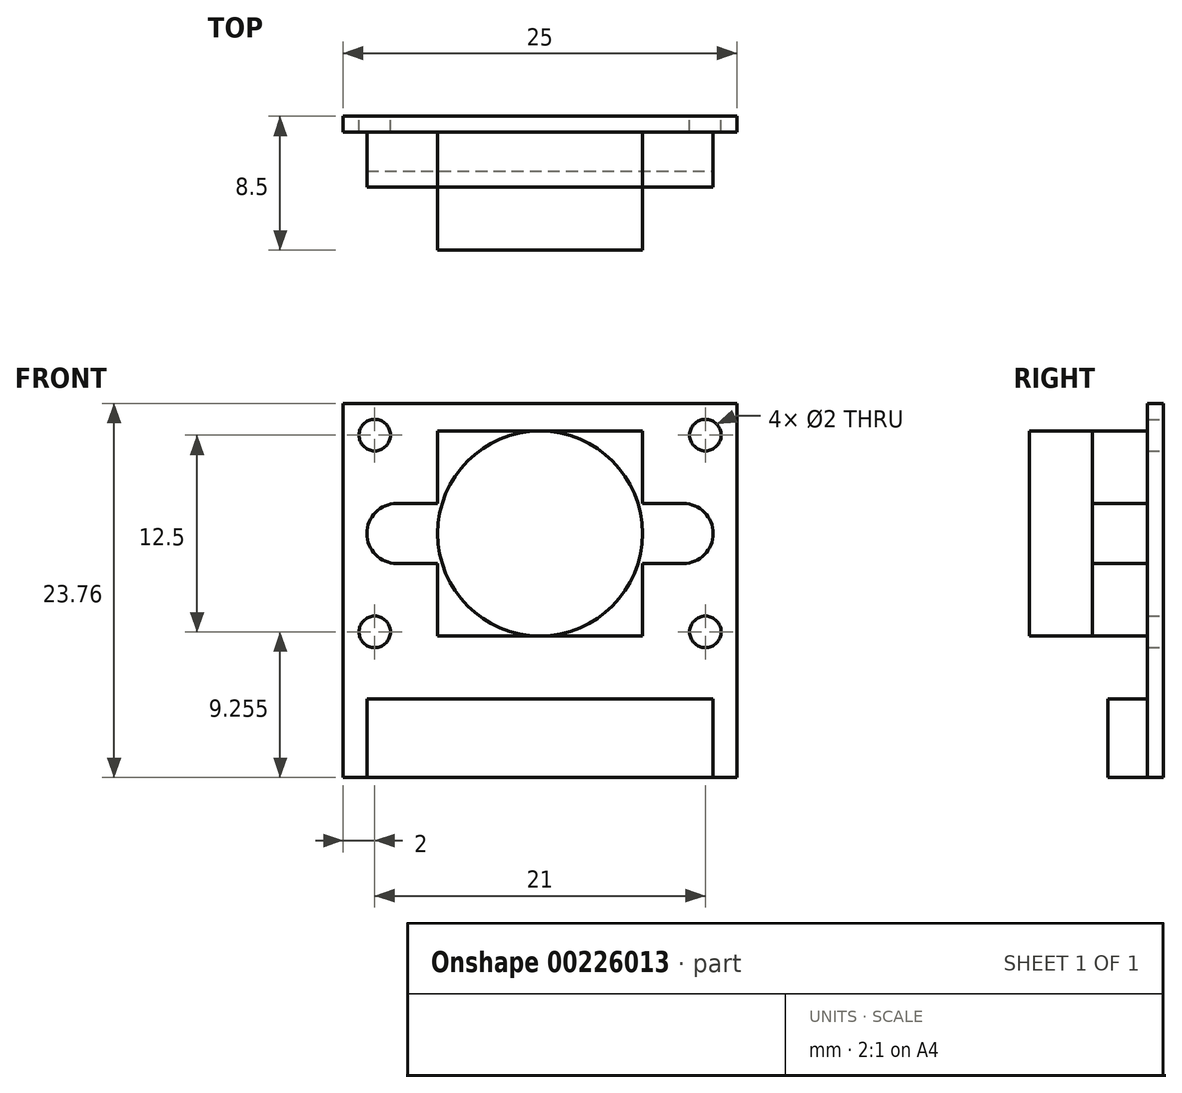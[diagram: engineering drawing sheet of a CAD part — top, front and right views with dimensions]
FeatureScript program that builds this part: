
annotation { "Feature Type Name" : "Feature", "Feature Type Description" : "" }
export const myFeature = defineFeature(function(context is Context, id is Id, definition is map)
    precondition{}
    {
        {
            var Q0;
            Q0=qCreatedBy(makeId("Front.planeOp"),FACE);
            var sketch = newSketch(context, id + "F0", { "sketchPlane" : qUnion([Q0])});
            skLineSegment(sketch, "E0.bottom", {"start": v(-12.5, 11.88) * mm, "end": v(12.5, 11.88) * mm});
            skLineSegment(sketch, "E0.top", {"start": v(-12.5, -11.88) * mm, "end": v(12.5, -11.88) * mm});
            skLineSegment(sketch, "E0.left", {"start": v(-12.5, 11.88) * mm, "end": v(-12.5, -11.87) * mm});
            skLineSegment(sketch, "E0.right", {"start": v(12.5, 11.88) * mm, "end": v(12.5, -11.87) * mm});
            skPoint(sketch, "E0.middle", {"position": v(0, 0) * mm});
            skCircle(sketch, "E1", {"center": v(-10.5, 9.87) * mm, "radius": 1 * mm});
            skLineSegment(sketch, "E2", {"start": v(0, 11.88) * mm, "end": v(0, 0) * mm, "construction": true});
            skCircle(sketch, "E3", {"center": v(-10.5, -2.63) * mm, "radius": 1 * mm});
            skCircle(sketch, "E4.MirrorC", {"center": v(10.5, 9.87) * mm, "radius": 1 * mm});
            skCircle(sketch, "E5.MirrorC", {"center": v(10.5, -2.63) * mm, "radius": 1 * mm});
            skSolve(sketch);
        }
        {
            var Q0;
            Q0 = qSketchRegion(id + "F0", true);
            extrude(context, id + "F1", {"entities" : qUnion([Q0]), "depth" : 1 * mm});
        }
        {
            var Q0;
            Q0=makeQuery(id+"F1.opExtrude","CAP_FACE",FACE,{"disambiguationData":[OSD([sQuery(id+"F0.wireOp",EDGE,"E0.bottom"),sQuery(id+"F0.wireOp",EDGE,"E0.top"),sQuery(id+"F0.wireOp",EDGE,"E0.left"),sQuery(id+"F0.wireOp",EDGE,"E0.right"),sQuery(id+"F0.wireOp",EDGE,"E1"),sQuery(id+"F0.wireOp",EDGE,"E3"),sQuery(id+"F0.wireOp",EDGE,"E4.MirrorC"),sQuery(id+"F0.wireOp",EDGE,"E5.MirrorC")])],"isStart":false});
            var sketch = newSketch(context, id + "F2", { "sketchPlane" : qUnion([Q0])});
            skLineSegment(sketch, "E6.bottom", {"start": v(-11, -11.88) * mm, "end": v(0, -11.88) * mm});
            skLineSegment(sketch, "E6.top", {"start": v(-11, -6.88) * mm, "end": v(0, -6.88) * mm});
            skLineSegment(sketch, "E6.left", {"start": v(-11, -11.88) * mm, "end": v(-11, -6.88) * mm});
            skLineSegment(sketch, "E7", {"start": v(0, 11.88) * mm, "end": v(0, -11.88) * mm, "construction": true});
            skLineSegment(sketch, "E8.MirrorCS", {"start": v(11, -6.88) * mm, "end": v(0, -6.88) * mm});
            skLineSegment(sketch, "E9.MirrorCS", {"start": v(11, -11.88) * mm, "end": v(11, -6.88) * mm});
            skLineSegment(sketch, "E10.MirrorCS", {"start": v(11, -11.88) * mm, "end": v(0, -11.88) * mm});
            skSolve(sketch);
        }
        {
            var Q0;
            Q0 = qSketchRegion(id + "F2", true);
            extrude(context, id + "F3", {"entities" : qUnion([Q0]), "depth" : 2.5 * mm});
        }
        {
            var Q0;
            Q0=makeQuery(id+"F1.opExtrude","CAP_FACE",FACE,{"disambiguationData":[OSD([sQuery(id+"F0.wireOp",EDGE,"E0.bottom"),sQuery(id+"F0.wireOp",EDGE,"E0.top"),sQuery(id+"F0.wireOp",EDGE,"E0.left"),sQuery(id+"F0.wireOp",EDGE,"E0.right"),sQuery(id+"F0.wireOp",EDGE,"E1"),sQuery(id+"F0.wireOp",EDGE,"E3"),sQuery(id+"F0.wireOp",EDGE,"E4.MirrorC"),sQuery(id+"F0.wireOp",EDGE,"E5.MirrorC")])],"isStart":false});
            var sketch = newSketch(context, id + "F4", { "sketchPlane" : qUnion([Q0])});
            skLineSegment(sketch, "E11.bottom", {"start": v(6.5, -2.88) * mm, "end": v(-6.5, -2.88) * mm});
            skLineSegment(sketch, "E11.top", {"start": v(6.5, 10.12) * mm, "end": v(-6.5, 10.12) * mm});
            skLineSegment(sketch, "E11.left", {"start": v(6.5, -2.88) * mm, "end": v(6.5, 1.72) * mm});
            skLineSegment(sketch, "E11.right", {"start": v(-6.5, -2.88) * mm, "end": v(-6.5, 1.72) * mm});
            skPoint(sketch, "E11.middle", {"position": v(0, 3.62) * mm});
            skLineSegment(sketch, "E12", {"start": v(0, 11.88) * mm, "end": v(0, 3.62) * mm, "construction": true});
            skPoint(sketch, "E12.endSnap0", {"position": v(0, 11.88) * mm});
            skLineSegment(sketch, "E13", {"start": v(-10.5, 9.87) * mm, "end": v(-10.5, -2.63) * mm, "construction": true});
            skLineSegment(sketch, "E14", {"start": v(-10.5, 3.62) * mm, "end": v(10.5, 3.62) * mm, "construction": true});
            skLineSegment(sketch, "E15", {"start": v(-9.1, 3.62) * mm, "end": v(9.1, 3.62) * mm, "construction": true});
            skArc(sketch, "E16.0.startCap", {"start": v(-9.1, 1.72) * mm, "mid": v(-11, 3.62) * mm, "end": v(-9.1, 5.52) * mm});
            skArc(sketch, "E16.0.endCap", {"start": v(9.1, 5.52) * mm, "mid": v(11, 3.62) * mm, "end": v(9.1, 1.72) * mm});
            skLineSegment(sketch, "E16.0.left", {"start": v(-9.1, 5.52) * mm, "end": v(-6.5, 5.52) * mm});
            skLineSegment(sketch, "E16.0.right", {"start": v(-9.1, 1.72) * mm, "end": v(-6.5, 1.72) * mm});
            skLineSegment(sketch, "E17.trimOffspring", {"start": v(-6.5, 5.52) * mm, "end": v(-6.5, 10.12) * mm});
            skLineSegment(sketch, "E18.trimOffspring", {"start": v(6.5, 5.52) * mm, "end": v(9.1, 5.52) * mm});
            skLineSegment(sketch, "E19.trimOffspring", {"start": v(6.5, 5.52) * mm, "end": v(6.5, 10.12) * mm});
            skLineSegment(sketch, "E20.trimOffspring", {"start": v(6.5, 1.72) * mm, "end": v(9.1, 1.72) * mm});
            skSolve(sketch);
        }
        {
            var Q0;
            Q0 = qSketchRegion(id + "F4", true);
            extrude(context, id + "F5", {"entities" : qUnion([Q0]), "depth" : 3.5 * mm});
        }
        {
            var Q0;
            Q0=makeQuery(id+"F5.opExtrude","CAP_FACE",FACE,{"disambiguationData":[OSD([sQuery(id+"F4.wireOp",EDGE,"E11.bottom"),sQuery(id+"F4.wireOp",EDGE,"E11.top"),sQuery(id+"F4.wireOp",EDGE,"E11.left"),sQuery(id+"F4.wireOp",EDGE,"E11.right"),sQuery(id+"F4.wireOp",EDGE,"E16.0.startCap"),sQuery(id+"F4.wireOp",EDGE,"E16.0.endCap"),sQuery(id+"F4.wireOp",EDGE,"E16.0.left"),sQuery(id+"F4.wireOp",EDGE,"E16.0.right"),sQuery(id+"F4.wireOp",EDGE,"E17.trimOffspring"),sQuery(id+"F4.wireOp",EDGE,"E18.trimOffspring"),sQuery(id+"F4.wireOp",EDGE,"E19.trimOffspring"),sQuery(id+"F4.wireOp",EDGE,"E20.trimOffspring")])],"isStart":false});
            var sketch = newSketch(context, id + "F6", { "sketchPlane" : qUnion([Q0])});
            skCircle(sketch, "E21", {"center": v(0, 3.62) * mm, "radius": 6.5 * mm});
            skPoint(sketch, "E21.centerSnap0", {"position": v(0, 10.12) * mm});
            skPoint(sketch, "E21.centerSnap1", {"position": v(-11, 3.62) * mm});
            skSolve(sketch);
        }
        {
            var Q0;
            Q0 = qSketchRegion(id + "F6", true);
            extrude(context, id + "F7", {"entities" : qUnion([Q0]), "operationType" : NewBodyOperationType.ADD, "depth" : 4 * mm});
        }
    });
